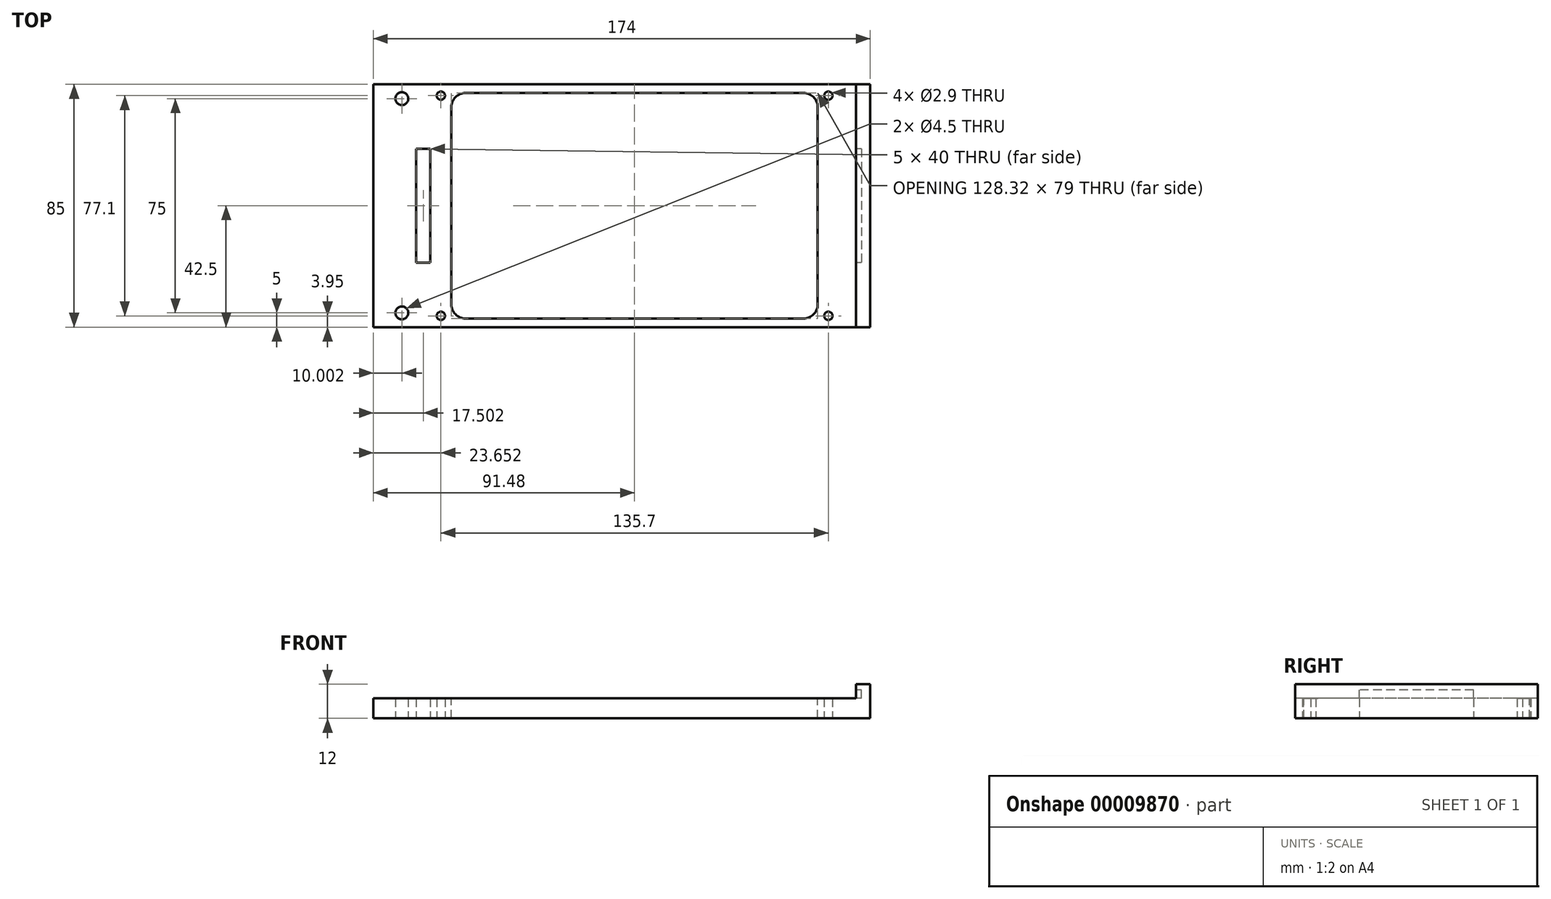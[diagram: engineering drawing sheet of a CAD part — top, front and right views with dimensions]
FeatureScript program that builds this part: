
annotation { "Feature Type Name" : "Feature", "Feature Type Description" : "" }
export const myFeature = defineFeature(function(context is Context, id is Id, definition is map)
    precondition{}
    {
        {
            var Q0;
            Q0=qCreatedBy(makeId("Top.planeOp"),FACE);
            var sketch = newSketch(context, id + "F0", { "sketchPlane" : qUnion([Q0])});
            skLineSegment(sketch, "E0.bottom", {"start": v(-31.79, 0) * mm, "end": v(111.21, 0) * mm});
            skLineSegment(sketch, "E0.top", {"start": v(-31.79, 85) * mm, "end": v(111.21, 85) * mm});
            skLineSegment(sketch, "E0.left", {"start": v(-31.79, 0) * mm, "end": v(-31.79, 85) * mm});
            skLineSegment(sketch, "E0.right", {"start": v(111.21, 0) * mm, "end": v(111.21, 85) * mm});
            skLineSegment(sketch, "E1.bottom", {"start": v(-31.79, 85) * mm, "end": v(-51.79, 85) * mm});
            skLineSegment(sketch, "E1.top", {"start": v(-31.79, 0) * mm, "end": v(-51.79, 0) * mm});
            skLineSegment(sketch, "E1.left", {"start": v(-31.79, 85) * mm, "end": v(-31.79, 0) * mm});
            skLineSegment(sketch, "E1.right", {"start": v(-51.79, 85) * mm, "end": v(-51.79, 0) * mm});
            skLineSegment(sketch, "E2.bottom", {"start": v(111.21, 85) * mm, "end": v(122.21, 85) * mm});
            skLineSegment(sketch, "E2.top", {"start": v(111.21, 0) * mm, "end": v(122.21, 0) * mm});
            skLineSegment(sketch, "E2.left", {"start": v(111.21, 85) * mm, "end": v(111.21, 0) * mm});
            skLineSegment(sketch, "E2.right", {"start": v(122.21, 85) * mm, "end": v(122.21, 0) * mm});
            skCircle(sketch, "E3", {"center": v(-41.79, 80) * mm, "radius": 2.25 * mm});
            skCircle(sketch, "E4", {"center": v(-41.79, 5) * mm, "radius": 2.25 * mm});
            skPoint(sketch, "E5", {"position": v(-41.79, 85) * mm});
            skLineSegment(sketch, "E6", {"start": v(-41.79, 5) * mm, "end": v(-41.79, 0) * mm});
            skLineSegment(sketch, "E7", {"start": v(-41.79, 80) * mm, "end": v(-41.79, 85) * mm});
            skCircle(sketch, "E8", {"center": v(-28.14, 81.05) * mm, "radius": 1.45 * mm});
            skCircle(sketch, "E9", {"center": v(-28.14, 3.95) * mm, "radius": 1.45 * mm});
            skCircle(sketch, "E10", {"center": v(107.56, 81.05) * mm, "radius": 1.45 * mm});
            skCircle(sketch, "E11", {"center": v(107.56, 3.95) * mm, "radius": 1.45 * mm});
            skLineSegment(sketch, "E12", {"start": v(-28.14, 81.05) * mm, "end": v(-31.79, 81.05) * mm});
            skLineSegment(sketch, "E13", {"start": v(-28.14, 81.05) * mm, "end": v(-28.14, 85) * mm});
            skLineSegment(sketch, "E14", {"start": v(107.56, 3.95) * mm, "end": v(107.56, 0) * mm});
            skLineSegment(sketch, "E15", {"start": v(107.56, 3.95) * mm, "end": v(111.21, 3.95) * mm});
            skLineSegment(sketch, "E16.bottom", {"start": v(-31.79, 62.5) * mm, "end": v(-36.79, 62.5) * mm});
            skLineSegment(sketch, "E16.top", {"start": v(-31.79, 22.5) * mm, "end": v(-36.79, 22.5) * mm});
            skLineSegment(sketch, "E16.left", {"start": v(-31.79, 62.5) * mm, "end": v(-31.79, 22.5) * mm});
            skLineSegment(sketch, "E16.right", {"start": v(-36.79, 62.5) * mm, "end": v(-36.79, 22.5) * mm});
            skPoint(sketch, "E17", {"position": v(-51.79, 42.5) * mm});
            skPoint(sketch, "E18", {"position": v(-36.79, 42.5) * mm});
            skLineSegment(sketch, "E19", {"start": v(117.21, 85) * mm, "end": v(117.21, 0) * mm});
            skSolve(sketch);
        }
        {
            var Q0;
            {var subQ0=sQuery(id+"F0.wireOp",EDGE,"E14");var subQ1=sQuery(id+"F0.wireOp",EDGE,"E11");var subQ2=makeQuery(id+"F0.imprint","INTERSECT",VERTEX,{"derivedFrom":[subQ1,subQ0]});Q0=makeQuery(id+"F0.imprint","IMPRINT",FACE,{"disambiguationData":[TD([[makeQuery(id+"F0.imprint","IMPRINT",EDGE,{"disambiguationData":[TD([[subQ2,-1.0]])],"derivedFrom":subQ1}),-1.0]])]});}
            var Q1;
            {var subQ0=sQuery(id+"F0.wireOp",EDGE,"E12");var subQ3=sQuery(id+"F0.wireOp",EDGE,"E8");var subQ4=makeQuery(id+"F0.imprint","INTERSECT",VERTEX,{"derivedFrom":[subQ3,subQ0]});Q1=makeQuery(id+"F0.imprint","IMPRINT",FACE,{"disambiguationData":[TD([[makeQuery(id+"F0.imprint","IMPRINT",EDGE,{"disambiguationData":[TD([[subQ4,1.0]])],"derivedFrom":subQ3}),-1.0]])]});}
            var Q2;
            {var subQ0=sQuery(id+"F0.wireOp",EDGE,"E1.right");Q2=makeQuery(id+"F0.imprint","IMPRINT",FACE,{"disambiguationData":[TD([[makeQuery(id+"F0.imprint","IMPRINT",EDGE,{"derivedFrom":subQ0}),1.0]])]});}
            var Q3;
            Q3=makeQuery(id+"F0.imprint","IMPRINT",FACE,{"disambiguationData":[TD([[makeQuery(id+"F0.imprint","IMPRINT",EDGE,{"derivedFrom":sQuery(id+"F0.wireOp",EDGE,"E9")}),-1.0]])]});
            var Q4;
            {var subQ6=sQuery(id+"F0.wireOp",EDGE,"E19");Q4=makeQuery(id+"F0.imprint","IMPRINT",FACE,{"disambiguationData":[TD([[makeQuery(id+"F0.imprint","IMPRINT",EDGE,{"derivedFrom":subQ6}),-1.0]])]});}
            extrude(context, id + "F1", {"entities" : qUnion([Q0, Q1, Q2, Q3, Q4]), "depth" : 7 * mm});
        }
        {
            var Q0;
            {var subQ3=sQuery(id+"F0.wireOp",EDGE,"E2.bottom");Q0=makeQuery(id+"F0.imprint","IMPRINT",FACE,{"disambiguationData":[TD([[makeQuery(id+"F0.imprint","IMPRINT",EDGE,{"derivedFrom":subQ3}),-1.0]])]});}
            extrude(context, id + "F2", {"entities" : qUnion([Q0]), "operationType" : NewBodyOperationType.ADD, "depth" : 12 * mm});
        }
        {
            var Q0;
            Q0=makeQuery(id+"F2.opExtrude","SWEPT_FACE",FACE,{"disambiguationData":[OSD([sQuery(id+"F0.wireOp",EDGE,"E19")])]});
            var sketch = newSketch(context, id + "F3", { "sketchPlane" : qUnion([Q0])});
            skLineSegment(sketch, "E20.bottom", {"start": v(-62.5, 7) * mm, "end": v(-22.5, 7) * mm});
            skLineSegment(sketch, "E20.top", {"start": v(-62.5, 10) * mm, "end": v(-22.5, 10) * mm});
            skLineSegment(sketch, "E20.left", {"start": v(-62.5, 7) * mm, "end": v(-62.5, 10) * mm});
            skLineSegment(sketch, "E20.right", {"start": v(-22.5, 7) * mm, "end": v(-22.5, 10) * mm});
            skPoint(sketch, "E21", {"position": v(-42.5, 12) * mm});
            skPoint(sketch, "E22", {"position": v(-42.5, 10) * mm});
            skSolve(sketch);
        }
        {
            var Q0;
            Q0 = qSketchRegion(id + "F3", true);
            extrude(context, id + "F4", {"entities" : qUnion([Q0]), "operationType" : NewBodyOperationType.REMOVE, "oppositeDirection" : true, "depth" : 2 * mm});
        }
        {
            var Q0;
            Q0=makeQuery(id+"F4.boolean.opBoolean","MERGE",FACE,{"derivedFrom":[makeQuery(id+"F1.opExtrude","CAP_FACE",FACE,{"disambiguationData":[OSD([sQuery(id+"F0.wireOp",EDGE,"E0.bottom"),sQuery(id+"F0.wireOp",EDGE,"E0.top"),sQuery(id+"F0.wireOp",EDGE,"E1.bottom"),sQuery(id+"F0.wireOp",EDGE,"E1.top"),sQuery(id+"F0.wireOp",EDGE,"E1.right"),sQuery(id+"F0.wireOp",EDGE,"E2.bottom"),sQuery(id+"F0.wireOp",EDGE,"E2.top"),sQuery(id+"F0.wireOp",EDGE,"E3"),sQuery(id+"F0.wireOp",EDGE,"E4"),sQuery(id+"F0.wireOp",EDGE,"E8"),sQuery(id+"F0.wireOp",EDGE,"E9"),sQuery(id+"F0.wireOp",EDGE,"E10"),sQuery(id+"F0.wireOp",EDGE,"E11"),sQuery(id+"F0.wireOp",EDGE,"E16.bottom"),sQuery(id+"F0.wireOp",EDGE,"E16.top"),sQuery(id+"F0.wireOp",EDGE,"E16.left"),sQuery(id+"F0.wireOp",EDGE,"E16.right"),sQuery(id+"F0.wireOp",EDGE,"E19")])],"isStart":false}),makeQuery(id+"F4.opExtrude","SWEPT_FACE",FACE,{"disambiguationData":[OSD([sQuery(id+"F3.wireOp",EDGE,"E20.bottom")])]})]});
            var sketch = newSketch(context, id + "F5", { "sketchPlane" : qUnion([Q0])});
            skLineSegment(sketch, "E23.bottom", {"start": v(-24.47, 82) * mm, "end": v(103.85, 82) * mm});
            skLineSegment(sketch, "E23.top", {"start": v(-24.47, 3) * mm, "end": v(103.85, 3) * mm});
            skLineSegment(sketch, "E23.left", {"start": v(-24.47, 82) * mm, "end": v(-24.47, 3) * mm});
            skLineSegment(sketch, "E23.right", {"start": v(103.85, 82) * mm, "end": v(103.85, 3) * mm});
            skSolve(sketch);
        }
        {
            var Q0;
            Q0 = qSketchRegion(id + "F5", true);
            extrude(context, id + "F6", {"entities" : qUnion([Q0]), "operationType" : NewBodyOperationType.REMOVE, "oppositeDirection" : true, "depth" : 25 * mm});
        }
        {
            var Q0;
            Q0=makeQuery(id+"F6.boolean.opBoolean","COPY",EDGE,{"derivedFrom":makeQuery(id+"F6.opExtrude","SWEPT_EDGE",EDGE,{"disambiguationData":[OSD([sQuery(id+"F5.wireOp",EDGE,"E23.bottom"),sQuery(id+"F5.wireOp",EDGE,"E23.left")])]})});
            var Q1;
            Q1=makeQuery(id+"F6.boolean.opBoolean","COPY",EDGE,{"derivedFrom":makeQuery(id+"F6.opExtrude","SWEPT_EDGE",EDGE,{"disambiguationData":[OSD([sQuery(id+"F5.wireOp",EDGE,"E23.bottom"),sQuery(id+"F5.wireOp",EDGE,"E23.right")])]})});
            var Q2;
            Q2=makeQuery(id+"F6.boolean.opBoolean","COPY",EDGE,{"derivedFrom":makeQuery(id+"F6.opExtrude","SWEPT_EDGE",EDGE,{"disambiguationData":[OSD([sQuery(id+"F5.wireOp",EDGE,"E23.top"),sQuery(id+"F5.wireOp",EDGE,"E23.right")])]})});
            var Q3;
            Q3=makeQuery(id+"F6.boolean.opBoolean","COPY",EDGE,{"derivedFrom":makeQuery(id+"F6.opExtrude","SWEPT_EDGE",EDGE,{"disambiguationData":[OSD([sQuery(id+"F5.wireOp",EDGE,"E23.top"),sQuery(id+"F5.wireOp",EDGE,"E23.left")])]})});
            fillet(context, id + "F7", {"entities" : qUnion([Q0, Q1, Q2, Q3]), "radius" : 5 * mm, "tangentPropagation" : true, "allowEdgeOverflow" : false});
        }
    });
